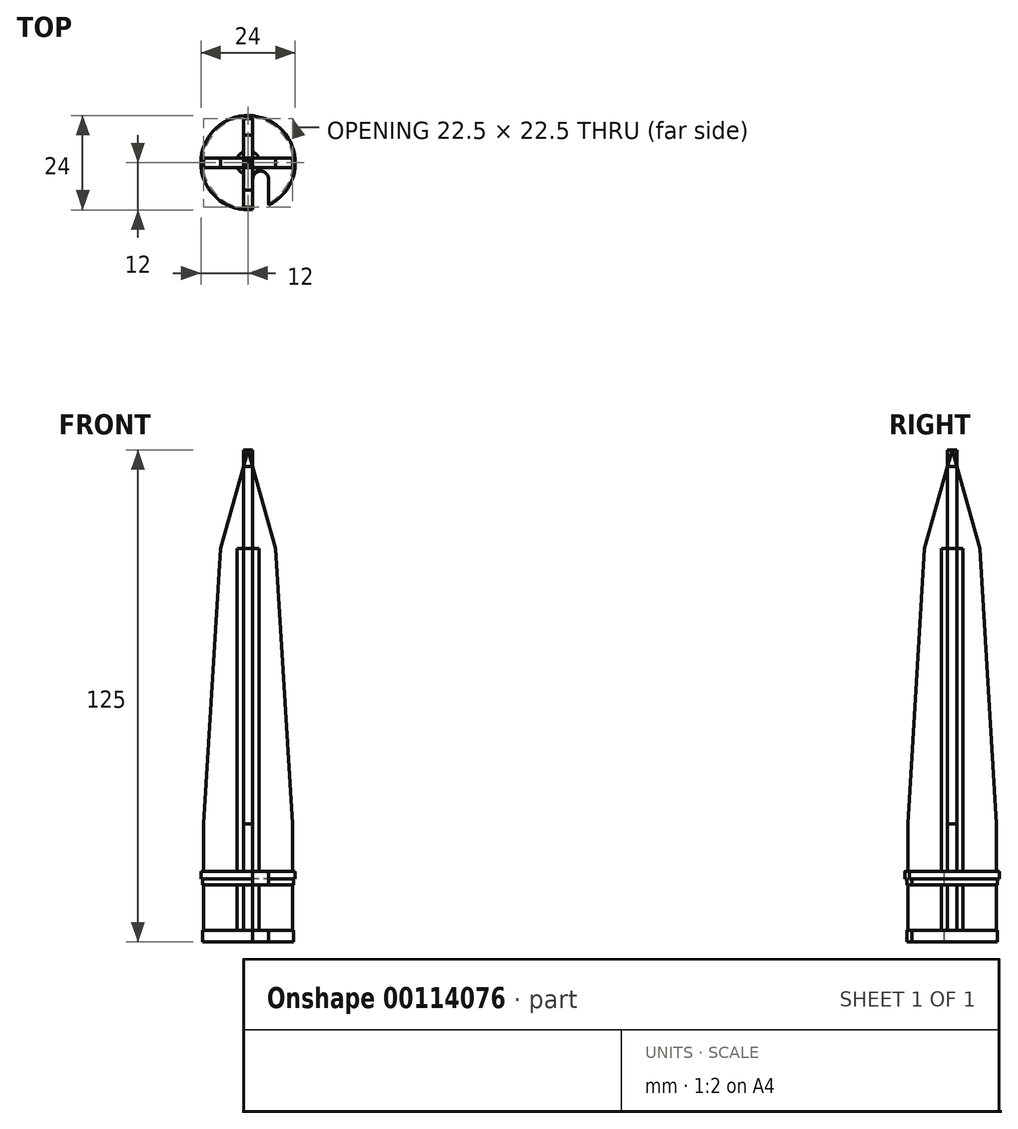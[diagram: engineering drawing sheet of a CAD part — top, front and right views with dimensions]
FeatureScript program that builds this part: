
annotation { "Feature Type Name" : "Feature", "Feature Type Description" : "" }
export const myFeature = defineFeature(function(context is Context, id is Id, definition is map)
    precondition{}
    {
        {
            var Q0;
            Q0=qCreatedBy(makeId("Top.planeOp"),FACE);
            var sketch = newSketch(context, id + "F0", { "sketchPlane" : qUnion([Q0])});
            skCircle(sketch, "E0", {"center": v(0, 0) * mm, "radius": 11.5 * mm});
            skCircle(sketch, "E1", {"center": v(0, 0) * mm, "radius": 12 * mm});
            skLineSegment(sketch, "E2", {"start": v(1.2, -11.94) * mm, "end": v(1.2, -4.14) * mm});
            skArc(sketch, "E3", {"start": v(5.2, -4.14) * mm, "mid": v(3.2, -2.14) * mm, "end": v(1.2, -4.14) * mm});
            skLineSegment(sketch, "E4", {"start": v(5.2, -4.14) * mm, "end": v(5.2, -11.94) * mm});
            skLineSegment(sketch, "E5", {"start": v(1.2, -11.94) * mm, "end": v(5.2, -11.94) * mm});
            skCircle(sketch, "E6", {"center": v(0, 0) * mm, "radius": 3 * mm});
            skSolve(sketch);
        }
        {
            var Q0;
            {var subQ1=sQuery(id+"F0.wireOp",EDGE,"E3");Q0=makeQuery(id+"F0.imprint","IMPRINT",FACE,{"disambiguationData":[TD([[makeQuery(id+"F0.imprint","IMPRINT",EDGE,{"derivedFrom":subQ1}),-1.0]])]});}
            var Q1;
            Q1=makeQuery(id+"F0.imprint","IMPRINT",FACE,{"disambiguationData":[TD([[makeQuery(id+"F0.imprint","IMPRINT",EDGE,{"derivedFrom":sQuery(id+"F0.wireOp",EDGE,"E6")}),1.0]])]});
            extrude(context, id + "F1", {"entities" : qUnion([Q0, Q1]), "depth" : 3 * mm});
        }
        {
            var Q0;
            Q0=makeQuery(id+"F1.opExtrude","CAP_FACE",FACE,{"disambiguationData":[OSD([sQuery(id+"F0.wireOp",EDGE,"E0")])],"isStart":true});
            extrude(context, id + "F2", {"entities" : qUnion([Q0]), "operationType" : NewBodyOperationType.ADD, "oppositeDirection" : true, "depth" : 16 * mm, "hasSecondDirection" : true, "secondDirectionOppositeDirection" : true, "secondDirectionDepth" : 14.5 * mm});
        }
        {
            var Q0;
            Q0=makeQuery(id+"F0.imprint","IMPRINT",FACE,{"disambiguationData":[TD([[makeQuery(id+"F0.imprint","IMPRINT",EDGE,{"derivedFrom":sQuery(id+"F0.wireOp",EDGE,"E6")}),1.0]])]});
            var Q1;
            {var subQ1=sQuery(id+"F0.wireOp",EDGE,"E3");Q1=makeQuery(id+"F0.imprint","IMPRINT",FACE,{"disambiguationData":[TD([[makeQuery(id+"F0.imprint","IMPRINT",EDGE,{"derivedFrom":subQ1}),-1.0]])]});}
            var Q2;
            {var subQ0=sQuery(id+"F0.wireOp",EDGE,"E2");var subQ1=sQuery(id+"F0.wireOp",EDGE,"E0");var subQ2=makeQuery(id+"F0.imprint","INTERSECT",VERTEX,{"derivedFrom":[subQ1,subQ0]});Q2=makeQuery(id+"F0.imprint","IMPRINT",FACE,{"disambiguationData":[TD([[makeQuery(id+"F0.imprint","IMPRINT",EDGE,{"disambiguationData":[TD([[subQ2,1.0]])],"derivedFrom":subQ1}),-1.0]])]});}
            extrude(context, id + "F3", {"entities" : qUnion([Q0, Q1, Q2]), "depth" : 18 * mm, "hasSecondDirection" : true, "secondDirectionOppositeDirection" : false, "secondDirectionDepth" : 16 * mm});
        }
        {
            var Q0;
            Q0=qCreatedBy(makeId("Front.planeOp"),FACE);
            var sketch = newSketch(context, id + "F4", { "sketchPlane" : qUnion([Q0])});
            skLineSegment(sketch, "E7", {"start": v(-11.25, 0) * mm, "end": v(-11.25, 30) * mm});
            skLineSegment(sketch, "E8", {"start": v(0, 100) * mm, "end": v(-7, 100) * mm, "construction": true});
            skLineSegment(sketch, "E9", {"start": v(-11.25, 30) * mm, "end": v(-7, 100) * mm});
            skLineSegment(sketch, "E10", {"start": v(-7, 100) * mm, "end": v(0, 125) * mm});
            skLineSegment(sketch, "E11", {"start": v(-11.25, 0) * mm, "end": v(0, 0) * mm});
            skLineSegment(sketch, "E12.MirrorCS", {"start": v(7, 100) * mm, "end": v(0, 125) * mm});
            skLineSegment(sketch, "E13.MirrorCS", {"start": v(11.25, 30) * mm, "end": v(7, 100) * mm});
            skLineSegment(sketch, "E14.MirrorCS", {"start": v(11.25, 0) * mm, "end": v(0, 0) * mm});
            skLineSegment(sketch, "E15.MirrorCS", {"start": v(11.25, 0) * mm, "end": v(11.25, 30) * mm});
            skSolve(sketch);
        }
        {
            var Q0;
            Q0=qCreatedBy(makeId("Right.planeOp"),FACE);
            var sketch = newSketch(context, id + "F5", { "sketchPlane" : qUnion([Q0])});
            skLineSegment(sketch, "E16", {"start": v(-11.25, 0) * mm, "end": v(-11.25, 30) * mm});
            skLineSegment(sketch, "E17", {"start": v(0, 100) * mm, "end": v(-7, 100) * mm, "construction": true});
            skLineSegment(sketch, "E18", {"start": v(-11.25, 30) * mm, "end": v(-7, 100) * mm});
            skLineSegment(sketch, "E19", {"start": v(-7, 100) * mm, "end": v(0, 125) * mm});
            skLineSegment(sketch, "E20", {"start": v(-11.25, 0) * mm, "end": v(0, 0) * mm});
            skLineSegment(sketch, "E21.MirrorCS", {"start": v(7, 100) * mm, "end": v(0, 125) * mm});
            skLineSegment(sketch, "E22.MirrorCS", {"start": v(11.25, 30) * mm, "end": v(7, 100) * mm});
            skLineSegment(sketch, "E23.MirrorCS", {"start": v(11.25, 0) * mm, "end": v(0, 0) * mm});
            skLineSegment(sketch, "E24.MirrorCS", {"start": v(11.25, 0) * mm, "end": v(11.25, 30) * mm});
            skSolve(sketch);
        }
        {
            var Q0;
            {var subQ5=sQuery(id+"F0.wireOp",EDGE,"E3");Q0=makeQuery(id+"F0.imprint","IMPRINT",FACE,{"disambiguationData":[TD([[makeQuery(id+"F0.imprint","IMPRINT",EDGE,{"derivedFrom":subQ5}),1.0]])]});}
            var Q1;
            {var subQ0=sQuery(id+"F0.wireOp",EDGE,"E2");var subQ1=sQuery(id+"F0.wireOp",EDGE,"E0");var subQ2=makeQuery(id+"F0.imprint","INTERSECT",VERTEX,{"derivedFrom":[subQ1,subQ0]});Q1=makeQuery(id+"F0.imprint","IMPRINT",FACE,{"disambiguationData":[TD([[makeQuery(id+"F0.imprint","IMPRINT",EDGE,{"disambiguationData":[TD([[subQ2,-1.0]])],"derivedFrom":subQ1}),-1.0]])]});}
            extrude(context, id + "F6", {"entities" : qUnion([Q0, Q1]), "operationType" : NewBodyOperationType.REMOVE, "endBound" : BoundingType.THROUGH_ALL, "depth" : 20 * mm});
        }
        {
            var Q0;
            Q0=makeQuery(id+"F4.imprint","IMPRINT",FACE,{"disambiguationData":[TD([[makeQuery(id+"F4.imprint","IMPRINT",EDGE,{"derivedFrom":sQuery(id+"F4.wireOp",EDGE,"E7")}),-1.0]])]});
            extrude(context, id + "F7", {"entities" : qUnion([Q0]), "endBound" : BoundingType.SYMMETRIC, "depth" : 2.35 * mm});
        }
        {
            var Q0;
            Q0=makeQuery(id+"F5.imprint","IMPRINT",FACE,{"disambiguationData":[TD([[makeQuery(id+"F5.imprint","IMPRINT",EDGE,{"derivedFrom":sQuery(id+"F5.wireOp",EDGE,"E16")}),-1.0]])]});
            extrude(context, id + "F8", {"entities" : qUnion([Q0]), "endBound" : BoundingType.SYMMETRIC, "depth" : 2.35 * mm});
        }
        {
            var Q0;
            Q0=makeQuery(id+"F0.imprint","IMPRINT",FACE,{"disambiguationData":[TD([[makeQuery(id+"F0.imprint","IMPRINT",EDGE,{"derivedFrom":sQuery(id+"F0.wireOp",EDGE,"E6")}),1.0]])]});
            extrude(context, id + "F9", {"entities" : qUnion([Q0]), "operationType" : NewBodyOperationType.ADD, "depth" : 100 * mm});
        }
    });
